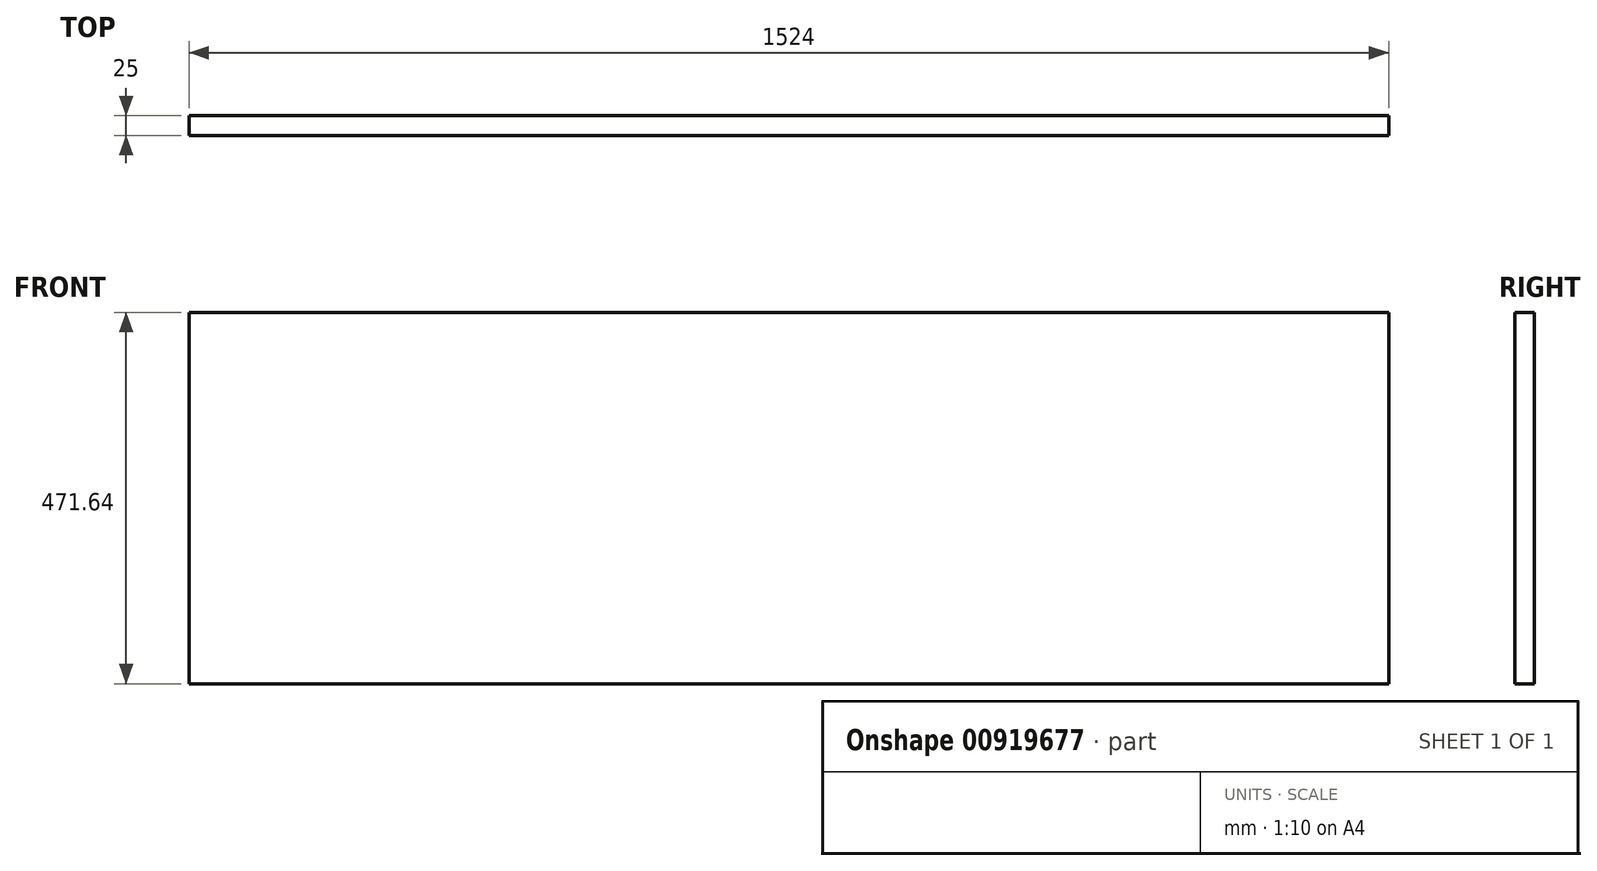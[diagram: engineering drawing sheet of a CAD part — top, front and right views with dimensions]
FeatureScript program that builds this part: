
annotation { "Feature Type Name" : "Feature", "Feature Type Description" : "" }
export const myFeature = defineFeature(function(context is Context, id is Id, definition is map)
    precondition{}
    {
        {
            var Q0;
            Q0=qCreatedBy(makeId("Front.planeOp"),FACE);
            var sketch = newSketch(context, id + "F0", { "sketchPlane" : qUnion([Q0])});
            skLineSegment(sketch, "E0.bottom", {"start": v(0, 0) * mm, "end": v(1524, 0) * mm});
            skLineSegment(sketch, "E0.top", {"start": v(0, 471.64) * mm, "end": v(1524, 471.64) * mm});
            skLineSegment(sketch, "E0.left", {"start": v(0, 0) * mm, "end": v(0, 471.64) * mm});
            skLineSegment(sketch, "E0.right", {"start": v(1524, 0) * mm, "end": v(1524, 471.64) * mm});
            skSolve(sketch);
        }
        {
            var Q0;
            Q0=makeQuery(id+"F0.imprint","IMPRINT",FACE,{"disambiguationData":[TD([[makeQuery(id+"F0.imprint","IMPRINT",EDGE,{"derivedFrom":sQuery(id+"F0.wireOp",EDGE,"E0.bottom")}),1.0]])]});
            extrude(context, id + "F1", {"entities" : qUnion([Q0]), "depth" : 25 * mm, "offsetDistance" : 25 * mm});
        }
    });
